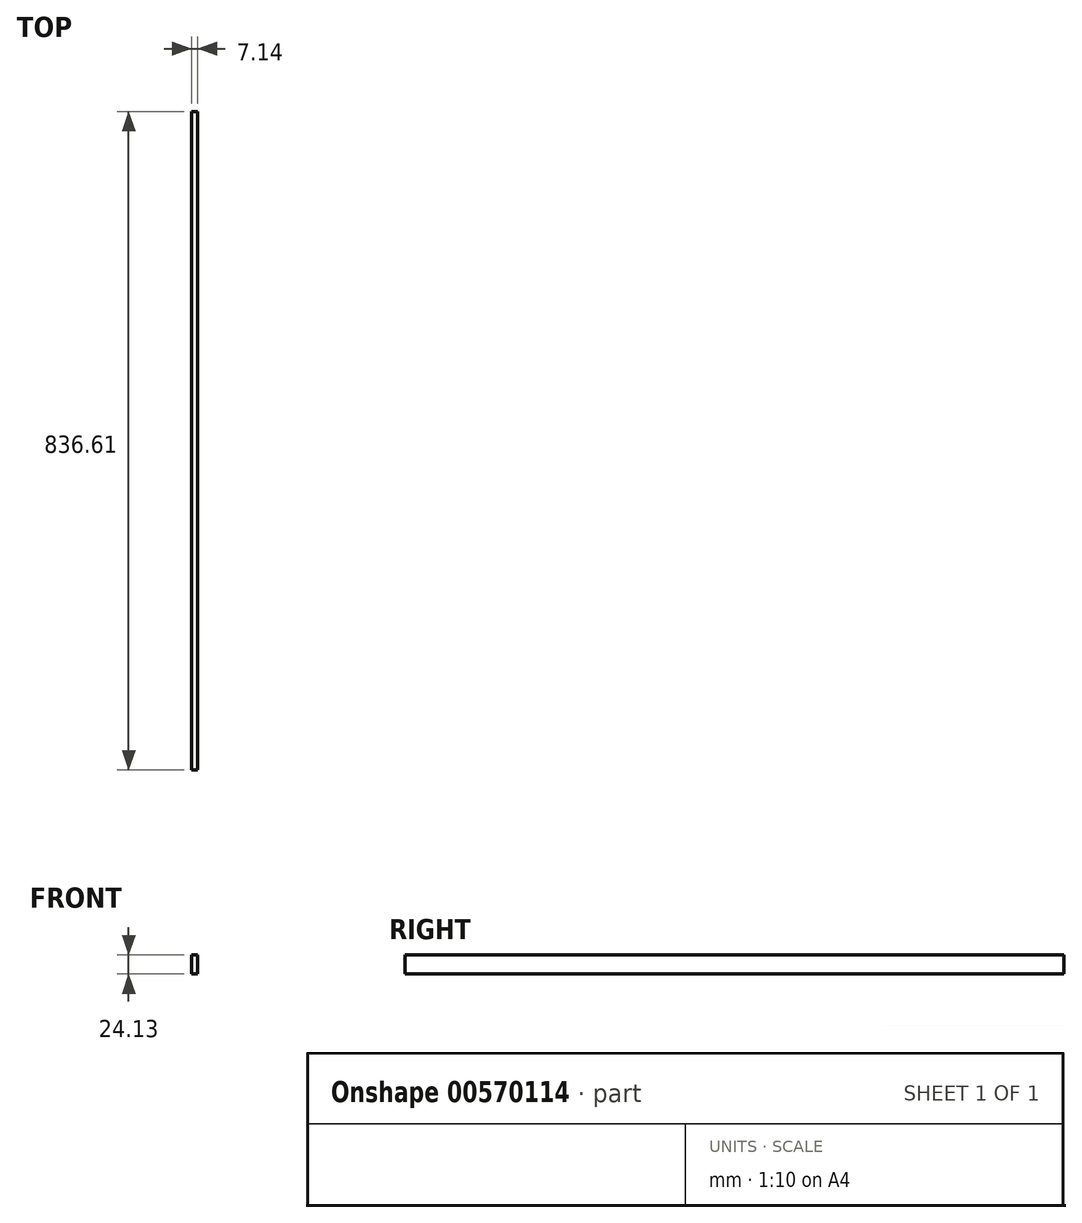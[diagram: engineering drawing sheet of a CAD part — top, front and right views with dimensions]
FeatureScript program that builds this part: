
annotation { "Feature Type Name" : "Feature", "Feature Type Description" : "" }
export const myFeature = defineFeature(function(context is Context, id is Id, definition is map)
    precondition{}
    {
        {
            var Q0;
            Q0=qCreatedBy(makeId("Front.planeOp"),FACE);
            var sketch = newSketch(context, id + "F0", { "sketchPlane" : qUnion([Q0])});
            skLineSegment(sketch, "E0.bottom", {"start": v(0, 0) * mm, "end": v(7.14, 0) * mm});
            skLineSegment(sketch, "E0.top", {"start": v(0, -24.13) * mm, "end": v(7.14, -24.13) * mm});
            skLineSegment(sketch, "E0.left", {"start": v(0, 0) * mm, "end": v(0, -24.13) * mm});
            skLineSegment(sketch, "E0.right", {"start": v(7.14, 0) * mm, "end": v(7.14, -24.13) * mm});
            skSolve(sketch);
        }
        {
            var Q0;
            Q0=makeQuery(id+"F0.imprint","IMPRINT",FACE,{"disambiguationData":[TD([[makeQuery(id+"F0.imprint","IMPRINT",EDGE,{"derivedFrom":sQuery(id+"F0.wireOp",EDGE,"E0.bottom")}),-1.0]])]});
            extrude(context, id + "F1", {"entities" : qUnion([Q0]), "depth" : 836.6 * mm, "offsetDistance" : 25.4 * mm});
        }
    });
